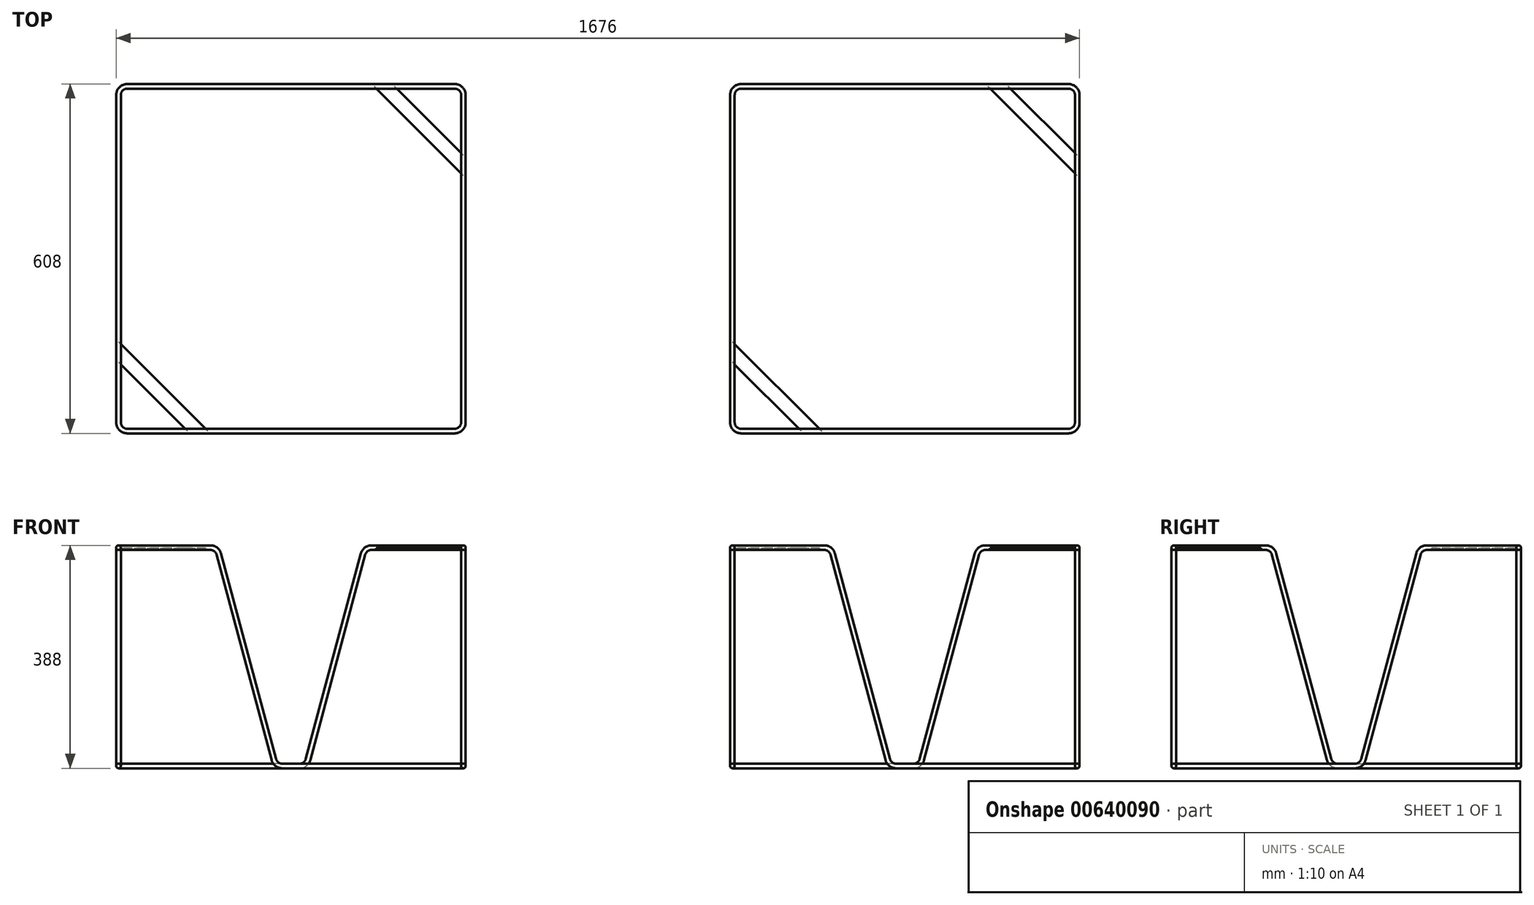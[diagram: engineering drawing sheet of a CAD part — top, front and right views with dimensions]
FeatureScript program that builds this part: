
annotation { "Feature Type Name" : "Feature", "Feature Type Description" : "" }
export const myFeature = defineFeature(function(context is Context, id is Id, definition is map)
    precondition{}
    {
        {
            var Q0;
            Q0=qCreatedBy(makeId("Top.planeOp"),FACE);
            var sketch = newSketch(context, id + "F0", { "sketchPlane" : qUnion([Q0])});
            skLineSegment(sketch, "E0.bottom", {"start": v(0, 0) * mm, "end": v(600, 0) * mm, "construction": true});
            skLineSegment(sketch, "E0.top", {"start": v(0, 600) * mm, "end": v(600, 600) * mm, "construction": true});
            skLineSegment(sketch, "E0.left", {"start": v(0, 0) * mm, "end": v(0, 600) * mm, "construction": true});
            skLineSegment(sketch, "E0.right", {"start": v(600, 0) * mm, "end": v(600, 600) * mm, "construction": true});
            skLineSegment(sketch, "E1", {"start": v(0, 600) * mm, "end": v(600, 0) * mm, "construction": true});
            skSolve(sketch);
        }
        {
            var Q0;
            Q0=sQuery(id+"F0.wireOp",EDGE,"E1");
            cPlane(context, id + "F1", {"entities" : qUnion([Q0]), "cplaneType" : CPlaneType.LINE_ANGLE, "offset" : 25 * mm, "angle" : 90 * degree, "oppositeDirection" : true, "width" : 150 * mm, "height" : 150 * mm});
        }
        {
            var Q0;
            Q0=qCreatedBy(makeId("Right.planeOp"),FACE);
            var sketch = newSketch(context, id + "F2", { "sketchPlane" : qUnion([Q0])});
            skLineSegment(sketch, "E2", {"start": v(0, 380) * mm, "end": v(160, 380) * mm, "construction": true});
            skLineSegment(sketch, "E3", {"start": v(174.49, 368.88) * mm, "end": v(270.35, 11.12) * mm});
            skLineSegment(sketch, "E4", {"start": v(284.84, 0) * mm, "end": v(600, 0) * mm, "construction": true});
            skLineSegment(sketch, "E5", {"start": v(0, 380) * mm, "end": v(0, 0) * mm, "construction": true});
            skPoint(sketch, "E6.visualSharp", {"position": v(171.5, 380) * mm});
            skArc(sketch, "E6.filletArc", {"start": v(174.49, 368.88) * mm, "mid": v(169.13, 376.9) * mm, "end": v(160, 380) * mm});
            skPoint(sketch, "E7.visualSharp", {"position": v(273.33, 0) * mm});
            skArc(sketch, "E7.filletArc", {"start": v(270.35, 11.12) * mm, "mid": v(275.7, 3.1) * mm, "end": v(284.84, 0) * mm});
            skSolve(sketch);
        }
        {
            var Q0;
            Q0=qCreatedBy(makeId("Front.planeOp"),FACE);
            var sketch = newSketch(context, id + "F3", { "sketchPlane" : qUnion([Q0])});
            skLineSegment(sketch, "E8.bottom", {"start": v(0, 0) * mm, "end": v(600, 0) * mm, "construction": true});
            skLineSegment(sketch, "E9", {"start": v(0, 380) * mm, "end": v(160, 380) * mm, "construction": true});
            skLineSegment(sketch, "E10", {"start": v(174.49, 368.88) * mm, "end": v(270.35, 11.12) * mm});
            skLineSegment(sketch, "E11", {"start": v(284.84, 0) * mm, "end": v(600, 0) * mm, "construction": true});
            skPoint(sketch, "E12.visualSharp", {"position": v(171.5, 380) * mm});
            skArc(sketch, "E12.filletArc", {"start": v(174.49, 368.88) * mm, "mid": v(169.13, 376.9) * mm, "end": v(160, 380) * mm});
            skPoint(sketch, "E13.visualSharp", {"position": v(273.33, 0) * mm});
            skArc(sketch, "E13.filletArc", {"start": v(270.35, 11.12) * mm, "mid": v(275.7, 3.1) * mm, "end": v(284.84, 0) * mm});
            skSolve(sketch);
        }
        {
            var Q0;
            Q0=qCreatedBy(makeId("Top.planeOp"),FACE);
            var Q1;
            Q1=sQuery(id+"F2.wireOp",VERTEX,"E5.start");
            cPlane(context, id + "F4", {"entities" : qUnion([Q0, Q1]), "cplaneType" : CPlaneType.PLANE_POINT, "offset" : 25 * mm, "width" : 150 * mm, "height" : 150 * mm});
        }
        {
            var Q0;
            Q0=qCreatedBy(id+"F4.planeOp",FACE);
            var sketch = newSketch(context, id + "F5", { "sketchPlane" : qUnion([Q0])});
            skLineSegment(sketch, "E14", {"start": v(0, 160) * mm, "end": v(0, 15) * mm});
            skLineSegment(sketch, "E15", {"start": v(15, 0) * mm, "end": v(160, 0) * mm});
            skPoint(sketch, "E16.visualSharp", {"position": v(0, 0) * mm});
            skArc(sketch, "E16.filletArc", {"start": v(0, 15) * mm, "mid": v(4.4, 4.4) * mm, "end": v(15, 0) * mm});
            skSolve(sketch);
        }
        {
            var Q0;
            Q0=qCreatedBy(makeId("Top.planeOp"),FACE);
            var sketch = newSketch(context, id + "F6", { "sketchPlane" : qUnion([Q0])});
            skLineSegment(sketch, "E17", {"start": v(0, 284.84) * mm, "end": v(0, 585) * mm});
            skPoint(sketch, "E18.visualSharp", {"position": v(0, 600) * mm});
            skArc(sketch, "E18.filletArc", {"start": v(4.4, 595.6) * mm, "mid": v(1.14, 590.74) * mm, "end": v(0, 585) * mm});
            skLineSegment(sketch, "E19", {"start": v(284.84, 0) * mm, "end": v(585, 0) * mm});
            skArc(sketch, "E20", {"start": v(585, 0) * mm, "mid": v(590.74, 1.14) * mm, "end": v(595.6, 4.4) * mm});
            skSolve(sketch);
        }
        {
            var Q0;
            Q0=qCreatedBy(id+"F1.planeOp",FACE);
            var sketch = newSketch(context, id + "F7", { "sketchPlane" : qUnion([Q0])});
            skCircle(sketch, "E21", {"center": v(418.05, 0) * mm, "radius": 4 * mm});
            skSolve(sketch);
        }
        {
            var Q0;
            Q0=makeQuery(id+"F7.imprint","IMPRINT",FACE,{"disambiguationData":[TD([[makeQuery(id+"F7.imprint","IMPRINT",EDGE,{"derivedFrom":sQuery(id+"F7.wireOp",EDGE,"E21")}),1.0]])]});
            var Q1;
            Q1=sQuery(id+"F6.wireOp",EDGE,"E20");
            var Q2;
            Q2=sQuery(id+"F6.wireOp",EDGE,"E19");
            var Q3;
            Q3=sQuery(id+"F3.wireOp",EDGE,"E13.filletArc");
            var Q4;
            Q4=sQuery(id+"F3.wireOp",EDGE,"E10");
            var Q5;
            Q5=sQuery(id+"F3.wireOp",EDGE,"E12.filletArc");
            var Q6;
            Q6=sQuery(id+"F5.wireOp",EDGE,"E15");
            var Q7;
            Q7=sQuery(id+"F5.wireOp",EDGE,"E16.filletArc");
            var Q8;
            Q8=sQuery(id+"F5.wireOp",EDGE,"E14");
            var Q9;
            Q9=sQuery(id+"F2.wireOp",EDGE,"E6.filletArc");
            var Q10;
            Q10=sQuery(id+"F2.wireOp",EDGE,"E3");
            var Q11;
            Q11=sQuery(id+"F2.wireOp",EDGE,"E7.filletArc");
            var Q12;
            Q12=sQuery(id+"F6.wireOp",EDGE,"E17");
            var Q13;
            Q13=sQuery(id+"F6.wireOp",EDGE,"E18.filletArc");
            sweep(context, id + "F8", {"profiles" : qUnion([Q0]), "path" : qUnion([Q1, Q2, Q3, Q4, Q5, Q6, Q7, Q8, Q9, Q10, Q11, Q12, Q13])});
        }
        {
            var Q0;
            Q0=qCreatedBy(id+"F4.planeOp",FACE);
            var sketch = newSketch(context, id + "F9", { "sketchPlane" : qUnion([Q0])});
            skLineSegment(sketch, "E22", {"start": v(120, 0) * mm, "end": v(0, 120) * mm});
            skLineSegment(sketch, "E23", {"start": v(0, 120) * mm, "end": v(0, 155.36) * mm});
            skLineSegment(sketch, "E24", {"start": v(0, 155.36) * mm, "end": v(155.36, 0) * mm});
            skLineSegment(sketch, "E25", {"start": v(155.36, 0) * mm, "end": v(120, 0) * mm});
            skSolve(sketch);
        }
        {
            var Q0;
            Q0 = qSketchRegion(id + "F9", true);
            extrude(context, id + "F10", {"entities" : qUnion([Q0]), "operationType" : NewBodyOperationType.ADD, "oppositeDirection" : true, "depth" : 4 * mm, "offsetDistance" : 25 * mm, "hasSecondDirection" : true, "secondDirectionOppositeDirection" : false, "secondDirectionDepth" : -1 * mm});
        }
        {
            var Q0;
            Q0=makeQuery(id+"F8.opSweep","SWEPT_BODY",BODY,{"disambiguationData":[OSD([sQuery(id+"F6.wireOp",EDGE,"E18.filletArc"),sQuery(id+"F7.wireOp",EDGE,"E21")])]});
            var Q1;
            Q1=qCreatedBy(id+"F1.planeOp",FACE);
            mirror(context, id + "F11", {"operationType" : NewBodyOperationType.ADD, "entities" : qUnion([Q0]), "mirrorPlane" : qUnion([Q1])});
        }
        {
            var Q0;
            Q0=makeQuery(id+"F8.opSweep","SWEPT_BODY",BODY,{"disambiguationData":[OSD([sQuery(id+"F6.wireOp",EDGE,"E18.filletArc"),sQuery(id+"F7.wireOp",EDGE,"E21")])]});
            transform(context, id + "F12", {"entities" : qUnion([Q0]), "transformType" : TransformType.TRANSLATION_3D, "dx" : 1068 * mm, "dy" : 0 * mm, "dz" : 0 * mm, "makeCopy" : true});
        }
    });
